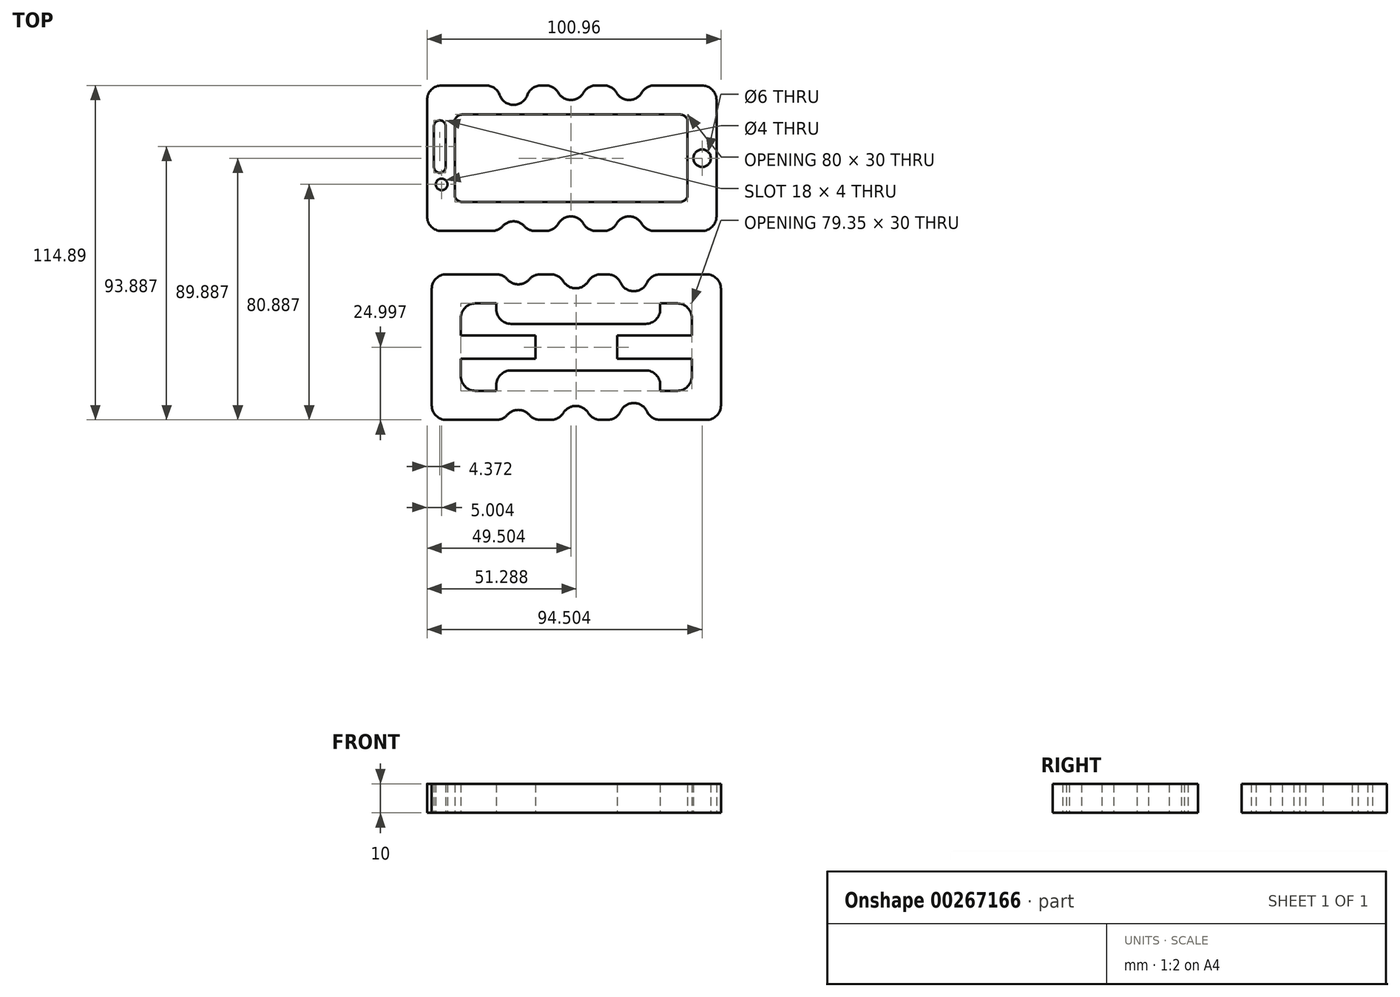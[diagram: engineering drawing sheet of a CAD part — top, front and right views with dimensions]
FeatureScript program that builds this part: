
annotation { "Feature Type Name" : "Feature", "Feature Type Description" : "" }
export const myFeature = defineFeature(function(context is Context, id is Id, definition is map)
    precondition{}
    {
        {
            var Q0;
            Q0=qCreatedBy(makeId("Top.planeOp"),FACE);
            var sketch = newSketch(context, id + "F0", { "sketchPlane" : qUnion([Q0])});
            skLineSegment(sketch, "E0", {"start": v(-47.02, 31.28) * mm, "end": v(-31.74, 31.28) * mm});
            skLineSegment(sketch, "E1", {"start": v(26.06, 31.28) * mm, "end": v(42.4, 31.28) * mm});
            skLineSegment(sketch, "E2", {"start": v(-52.02, 26.28) * mm, "end": v(-52.02, -13.72) * mm});
            skLineSegment(sketch, "E3", {"start": v(47.4, 26.28) * mm, "end": v(47.4, -13.72) * mm});
            skLineSegment(sketch, "E4", {"start": v(-47.02, -18.72) * mm, "end": v(-29.74, -18.72) * mm});
            skLineSegment(sketch, "E5", {"start": v(26.06, -18.72) * mm, "end": v(42.4, -18.72) * mm});
            skArc(sketch, "E6", {"start": v(-27.03, 27.93) * mm, "mid": v(-22.3, 24.59) * mm, "end": v(-17.6, 27.93) * mm});
            skArc(sketch, "E7", {"start": v(-6.93, 28.78) * mm, "mid": v(-2.6, 26.28) * mm, "end": v(1.73, 28.78) * mm});
            skArc(sketch, "E8", {"start": v(13.07, 28.78) * mm, "mid": v(17.4, 26.28) * mm, "end": v(21.73, 28.78) * mm});
            skArc(sketch, "E9", {"start": v(21.73, -16.22) * mm, "mid": v(17.4, -13.72) * mm, "end": v(13.07, -16.22) * mm});
            skArc(sketch, "E10", {"start": v(1.73, -16.22) * mm, "mid": v(-2.6, -13.72) * mm, "end": v(-6.93, -16.22) * mm});
            skArc(sketch, "E11", {"start": v(-18.6, -17.07) * mm, "mid": v(-22.3, -15.41) * mm, "end": v(-26.03, -17.07) * mm});
            skLineSegment(sketch, "E12", {"start": v(-12.87, 31.28) * mm, "end": v(-11.26, 31.28) * mm});
            skLineSegment(sketch, "E13", {"start": v(6.06, 31.28) * mm, "end": v(8.74, 31.28) * mm});
            skLineSegment(sketch, "E14", {"start": v(8.74, -18.72) * mm, "end": v(6.06, -18.72) * mm});
            skLineSegment(sketch, "E15", {"start": v(-11.26, -18.72) * mm, "end": v(-14.87, -18.72) * mm});
            skArc(sketch, "E16.filletArc", {"start": v(-12.87, 31.28) * mm, "mid": v(-15.77, 30.36) * mm, "end": v(-17.6, 27.93) * mm});
            skArc(sketch, "E17.filletArc", {"start": v(-6.93, 28.78) * mm, "mid": v(-8.76, 30.6) * mm, "end": v(-11.26, 31.28) * mm});
            skArc(sketch, "E18.filletArc", {"start": v(6.06, 31.28) * mm, "mid": v(3.56, 30.6) * mm, "end": v(1.73, 28.78) * mm});
            skArc(sketch, "E19.filletArc", {"start": v(13.07, 28.78) * mm, "mid": v(11.24, 30.6) * mm, "end": v(8.74, 31.28) * mm});
            skArc(sketch, "E20.filletArc", {"start": v(-18.6, -17.07) * mm, "mid": v(-16.9, -18.3) * mm, "end": v(-14.87, -18.72) * mm});
            skArc(sketch, "E21.filletArc", {"start": v(-11.26, -18.72) * mm, "mid": v(-8.76, -18.05) * mm, "end": v(-6.93, -16.22) * mm});
            skArc(sketch, "E22.filletArc", {"start": v(1.73, -16.22) * mm, "mid": v(3.56, -18.05) * mm, "end": v(6.06, -18.72) * mm});
            skArc(sketch, "E23.filletArc", {"start": v(8.74, -18.72) * mm, "mid": v(11.24, -18.05) * mm, "end": v(13.07, -16.22) * mm});
            skPoint(sketch, "E24.start.orphan", {"position": v(18.7, 26.45) * mm});
            skArc(sketch, "E25.filletArc", {"start": v(-27.03, 27.93) * mm, "mid": v(-28.85, 30.36) * mm, "end": v(-31.74, 31.28) * mm});
            skArc(sketch, "E26.filletArc", {"start": v(26.06, 31.28) * mm, "mid": v(23.56, 30.6) * mm, "end": v(21.73, 28.78) * mm});
            skArc(sketch, "E27.filletArc", {"start": v(21.73, -16.22) * mm, "mid": v(23.56, -18.05) * mm, "end": v(26.06, -18.72) * mm});
            skArc(sketch, "E28.filletArc", {"start": v(-29.74, -18.72) * mm, "mid": v(-27.7, -18.3) * mm, "end": v(-26.03, -17.07) * mm});
            skLineSegment(sketch, "E29", {"start": v(-42.52, 18.78) * mm, "end": v(-42.52, -6.22) * mm});
            skLineSegment(sketch, "E30", {"start": v(37.48, -6.22) * mm, "end": v(37.48, 18.78) * mm});
            skLineSegment(sketch, "E31", {"start": v(34.98, -8.72) * mm, "end": v(-40.02, -8.72) * mm});
            skCircle(sketch, "E32", {"center": v(42.48, 6.28) * mm, "radius": 3 * mm});
            skArc(sketch, "E33.filletArc", {"start": v(-47.02, 31.28) * mm, "mid": v(-50.55, 29.81) * mm, "end": v(-52.02, 26.28) * mm});
            skArc(sketch, "E34.filletArc", {"start": v(-52.02, -13.72) * mm, "mid": v(-50.55, -17.26) * mm, "end": v(-47.02, -18.72) * mm});
            skArc(sketch, "E35.filletArc", {"start": v(42.4, -18.72) * mm, "mid": v(45.93, -17.26) * mm, "end": v(47.4, -13.72) * mm});
            skArc(sketch, "E36.filletArc", {"start": v(47.4, 26.28) * mm, "mid": v(45.93, 29.81) * mm, "end": v(42.4, 31.28) * mm});
            skLineSegment(sketch, "E37", {"start": v(-40.02, 21.28) * mm, "end": v(34.98, 21.28) * mm});
            skArc(sketch, "E38.filletArc", {"start": v(-42.52, -6.22) * mm, "mid": v(-41.78, -8) * mm, "end": v(-40.02, -8.72) * mm});
            skArc(sketch, "E39.filletArc", {"start": v(34.98, -8.72) * mm, "mid": v(36.75, -8) * mm, "end": v(37.48, -6.22) * mm});
            skArc(sketch, "E40.filletArc", {"start": v(37.48, 18.78) * mm, "mid": v(36.75, 20.54) * mm, "end": v(34.98, 21.28) * mm});
            skPoint(sketch, "E41", {"position": v(-47.02, -2.72) * mm});
            skCircle(sketch, "E42", {"center": v(-47.02, -2.72) * mm, "radius": 2 * mm});
            skPoint(sketch, "E43", {"position": v(-47.65, 1.28) * mm});
            skLineSegment(sketch, "E44", {"start": v(-47.65, 1.28) * mm, "end": v(-47.65, 1.28) * mm});
            skLineSegment(sketch, "E45", {"start": v(-49.65, 3.28) * mm, "end": v(-49.65, 17.28) * mm});
            skLineSegment(sketch, "E46", {"start": v(-45.65, 3.28) * mm, "end": v(-45.65, 17.28) * mm});
            skLineSegment(sketch, "E47", {"start": v(-47.65, 19.28) * mm, "end": v(-47.65, 19.28) * mm});
            skArc(sketch, "E48.filletArc", {"start": v(-47.65, 19.28) * mm, "mid": v(-49.06, 18.7) * mm, "end": v(-49.65, 17.28) * mm});
            skArc(sketch, "E49.filletArc", {"start": v(-49.65, 3.28) * mm, "mid": v(-49.06, 1.86) * mm, "end": v(-47.65, 1.28) * mm});
            skArc(sketch, "E50.filletArc", {"start": v(-47.65, 1.28) * mm, "mid": v(-46.23, 1.86) * mm, "end": v(-45.65, 3.28) * mm});
            skArc(sketch, "E51.filletArc", {"start": v(-45.65, 17.28) * mm, "mid": v(-46.23, 18.7) * mm, "end": v(-47.65, 19.28) * mm});
            skArc(sketch, "E52.filletArc", {"start": v(-40.02, 21.28) * mm, "mid": v(-41.78, 20.54) * mm, "end": v(-42.52, 18.78) * mm});
            skLineSegment(sketch, "E53", {"start": v(-45.4, -33.61) * mm, "end": v(-28.2, -33.61) * mm});
            skLineSegment(sketch, "E54", {"start": v(-13.14, -33.61) * mm, "end": v(-9.47, -33.61) * mm});
            skLineSegment(sketch, "E55", {"start": v(7.61, -33.61) * mm, "end": v(9.94, -33.61) * mm});
            skLineSegment(sketch, "E56", {"start": v(28.08, -33.61) * mm, "end": v(43.94, -33.61) * mm});
            skLineSegment(sketch, "E57", {"start": v(48.94, -38.61) * mm, "end": v(48.94, -78.61) * mm});
            skLineSegment(sketch, "E58", {"start": v(43.94, -83.61) * mm, "end": v(28.08, -83.61) * mm});
            skLineSegment(sketch, "E59", {"start": v(9.94, -83.61) * mm, "end": v(7.61, -83.61) * mm});
            skLineSegment(sketch, "E60", {"start": v(-9.47, -83.61) * mm, "end": v(-13.14, -83.61) * mm});
            skLineSegment(sketch, "E61", {"start": v(-28.2, -83.61) * mm, "end": v(-45.4, -83.61) * mm});
            skLineSegment(sketch, "E62", {"start": v(-50.4, -38.61) * mm, "end": v(-50.4, -43.61) * mm});
            skLineSegment(sketch, "E63", {"start": v(-50.4, -43.61) * mm, "end": v(-50.4, -73.61) * mm});
            skLineSegment(sketch, "E64", {"start": v(-50.4, -73.61) * mm, "end": v(-50.4, -78.61) * mm});
            skArc(sketch, "E65", {"start": v(-24.43, -35.32) * mm, "mid": v(-20.67, -37.03) * mm, "end": v(-16.9, -35.32) * mm});
            skArc(sketch, "E66", {"start": v(-5.2, -36.01) * mm, "mid": v(-0.93, -38.4) * mm, "end": v(3.34, -36.01) * mm});
            skArc(sketch, "E67", {"start": v(14.47, -36.5) * mm, "mid": v(19, -39.4) * mm, "end": v(23.54, -36.5) * mm});
            skArc(sketch, "E68", {"start": v(23.54, -80.72) * mm, "mid": v(19, -77.82) * mm, "end": v(14.47, -80.72) * mm});
            skArc(sketch, "E69", {"start": v(3.34, -81.22) * mm, "mid": v(-0.93, -78.82) * mm, "end": v(-5.2, -81.22) * mm});
            skArc(sketch, "E70", {"start": v(-16.9, -81.9) * mm, "mid": v(-20.67, -80.2) * mm, "end": v(-24.43, -81.9) * mm});
            skArc(sketch, "E71.filletArc", {"start": v(-16.9, -81.9) * mm, "mid": v(-15.2, -83.17) * mm, "end": v(-13.14, -83.61) * mm});
            skArc(sketch, "E72.filletArc", {"start": v(-9.47, -83.61) * mm, "mid": v(-7.02, -82.97) * mm, "end": v(-5.2, -81.22) * mm});
            skArc(sketch, "E73.filletArc", {"start": v(3.34, -81.22) * mm, "mid": v(5.16, -82.97) * mm, "end": v(7.61, -83.61) * mm});
            skArc(sketch, "E74.filletArc", {"start": v(9.94, -83.61) * mm, "mid": v(12.63, -82.83) * mm, "end": v(14.47, -80.72) * mm});
            skArc(sketch, "E75.filletArc", {"start": v(23.54, -80.72) * mm, "mid": v(25.39, -82.83) * mm, "end": v(28.08, -83.61) * mm});
            skArc(sketch, "E76.filletArc", {"start": v(-28.2, -83.61) * mm, "mid": v(-26.13, -83.17) * mm, "end": v(-24.43, -81.9) * mm});
            skArc(sketch, "E77.filletArc", {"start": v(-24.43, -35.32) * mm, "mid": v(-26.13, -34.06) * mm, "end": v(-28.2, -33.61) * mm});
            skArc(sketch, "E78.filletArc", {"start": v(28.08, -33.61) * mm, "mid": v(25.39, -34.4) * mm, "end": v(23.54, -36.5) * mm});
            skArc(sketch, "E79.filletArc", {"start": v(14.47, -36.5) * mm, "mid": v(12.63, -34.4) * mm, "end": v(9.94, -33.61) * mm});
            skArc(sketch, "E80.filletArc", {"start": v(-13.14, -33.61) * mm, "mid": v(-15.2, -34.06) * mm, "end": v(-16.9, -35.32) * mm});
            skArc(sketch, "E81.filletArc", {"start": v(-5.2, -36.01) * mm, "mid": v(-7.02, -34.25) * mm, "end": v(-9.47, -33.61) * mm});
            skArc(sketch, "E82.filletArc", {"start": v(7.61, -33.61) * mm, "mid": v(5.16, -34.25) * mm, "end": v(3.34, -36.01) * mm});
            skArc(sketch, "E83.filletArc", {"start": v(-45.4, -33.61) * mm, "mid": v(-48.94, -35.08) * mm, "end": v(-50.4, -38.61) * mm});
            skArc(sketch, "E84.filletArc", {"start": v(-50.4, -78.61) * mm, "mid": v(-48.94, -82.15) * mm, "end": v(-45.4, -83.61) * mm});
            skArc(sketch, "E85.filletArc", {"start": v(43.94, -83.61) * mm, "mid": v(47.48, -82.15) * mm, "end": v(48.94, -78.61) * mm});
            skArc(sketch, "E86.filletArc", {"start": v(48.94, -38.61) * mm, "mid": v(47.48, -35.08) * mm, "end": v(43.94, -33.61) * mm});
            skLineSegment(sketch, "E87", {"start": v(-40.4, -48.61) * mm, "end": v(-40.4, -54.61) * mm});
            skLineSegment(sketch, "E88", {"start": v(-35.4, -43.61) * mm, "end": v(-28.2, -43.61) * mm});
            skLineSegment(sketch, "E89", {"start": v(-35.4, -73.61) * mm, "end": v(-28.2, -73.61) * mm});
            skLineSegment(sketch, "E90", {"start": v(38.94, -48.61) * mm, "end": v(38.94, -54.61) * mm});
            skLineSegment(sketch, "E91", {"start": v(33.94, -43.61) * mm, "end": v(28.08, -43.61) * mm});
            skLineSegment(sketch, "E92", {"start": v(33.94, -73.61) * mm, "end": v(28.08, -73.61) * mm});
            skLineSegment(sketch, "E93", {"start": v(0, -50.61) * mm, "end": v(-23.2, -50.61) * mm});
            skLineSegment(sketch, "E94", {"start": v(-28.2, -45.61) * mm, "end": v(-28.2, -43.61) * mm});
            skLineSegment(sketch, "E95", {"start": v(0, -66.61) * mm, "end": v(-23.2, -66.61) * mm});
            skLineSegment(sketch, "E96", {"start": v(-28.2, -71.61) * mm, "end": v(-28.2, -73.61) * mm});
            skLineSegment(sketch, "E97", {"start": v(0, -50.61) * mm, "end": v(23.08, -50.61) * mm});
            skLineSegment(sketch, "E98", {"start": v(28.08, -45.61) * mm, "end": v(28.08, -43.61) * mm});
            skLineSegment(sketch, "E99", {"start": v(0, -66.61) * mm, "end": v(23.08, -66.61) * mm});
            skLineSegment(sketch, "E100", {"start": v(28.08, -71.61) * mm, "end": v(28.08, -73.61) * mm});
            skArc(sketch, "E101.filletArc", {"start": v(-35.4, -43.61) * mm, "mid": v(-38.94, -45.08) * mm, "end": v(-40.4, -48.61) * mm});
            skArc(sketch, "E102.filletArc", {"start": v(-40.4, -68.61) * mm, "mid": v(-38.94, -72.15) * mm, "end": v(-35.4, -73.61) * mm});
            skArc(sketch, "E103.filletArc", {"start": v(33.94, -73.61) * mm, "mid": v(37.48, -72.15) * mm, "end": v(38.94, -68.61) * mm});
            skArc(sketch, "E104.filletArc", {"start": v(38.94, -48.61) * mm, "mid": v(37.48, -45.08) * mm, "end": v(33.94, -43.61) * mm});
            skArc(sketch, "E105.filletArc", {"start": v(28.08, -71.61) * mm, "mid": v(26.61, -68.08) * mm, "end": v(23.08, -66.61) * mm});
            skArc(sketch, "E106.filletArc", {"start": v(-23.2, -66.61) * mm, "mid": v(-26.73, -68.08) * mm, "end": v(-28.2, -71.61) * mm});
            skArc(sketch, "E107.filletArc", {"start": v(-28.2, -45.61) * mm, "mid": v(-26.73, -49.15) * mm, "end": v(-23.2, -50.61) * mm});
            skArc(sketch, "E108.filletArc", {"start": v(23.08, -50.61) * mm, "mid": v(26.61, -49.15) * mm, "end": v(28.08, -45.61) * mm});
            skLineSegment(sketch, "E109", {"start": v(-28.4, -54.61) * mm, "end": v(-14.73, -54.61) * mm});
            skLineSegment(sketch, "E110", {"start": v(26.94, -62.61) * mm, "end": v(13.27, -62.61) * mm});
            skLineSegment(sketch, "E111.trimOffspring", {"start": v(-40.4, -62.61) * mm, "end": v(-40.4, -68.61) * mm});
            skLineSegment(sketch, "E112.trimOffspring", {"start": v(38.94, -62.61) * mm, "end": v(38.94, -68.61) * mm});
            skLineSegment(sketch, "E113", {"start": v(-40.4, -54.61) * mm, "end": v(-28.4, -54.61) * mm});
            skLineSegment(sketch, "E114", {"start": v(-28.4, -62.61) * mm, "end": v(-40.4, -62.61) * mm});
            skLineSegment(sketch, "E115", {"start": v(26.94, -54.61) * mm, "end": v(38.94, -54.61) * mm});
            skLineSegment(sketch, "E116", {"start": v(38.94, -62.61) * mm, "end": v(26.94, -62.61) * mm});
            skLineSegment(sketch, "E117", {"start": v(-14.73, -54.61) * mm, "end": v(-14.73, -62.61) * mm});
            skLineSegment(sketch, "E118", {"start": v(13.27, -54.61) * mm, "end": v(13.27, -62.61) * mm});
            skLineSegment(sketch, "E119.trimOffspring", {"start": v(13.27, -54.61) * mm, "end": v(26.94, -54.61) * mm});
            skLineSegment(sketch, "E120.trimOffspring", {"start": v(-14.73, -62.61) * mm, "end": v(-28.4, -62.61) * mm});
            skSolve(sketch);
        }
        {
            var Q0;
            Q0 = qSketchRegion(id + "F0", true);
            extrude(context, id + "F1", {"entities" : qUnion([Q0]), "depth" : 10 * mm});
        }
    });
